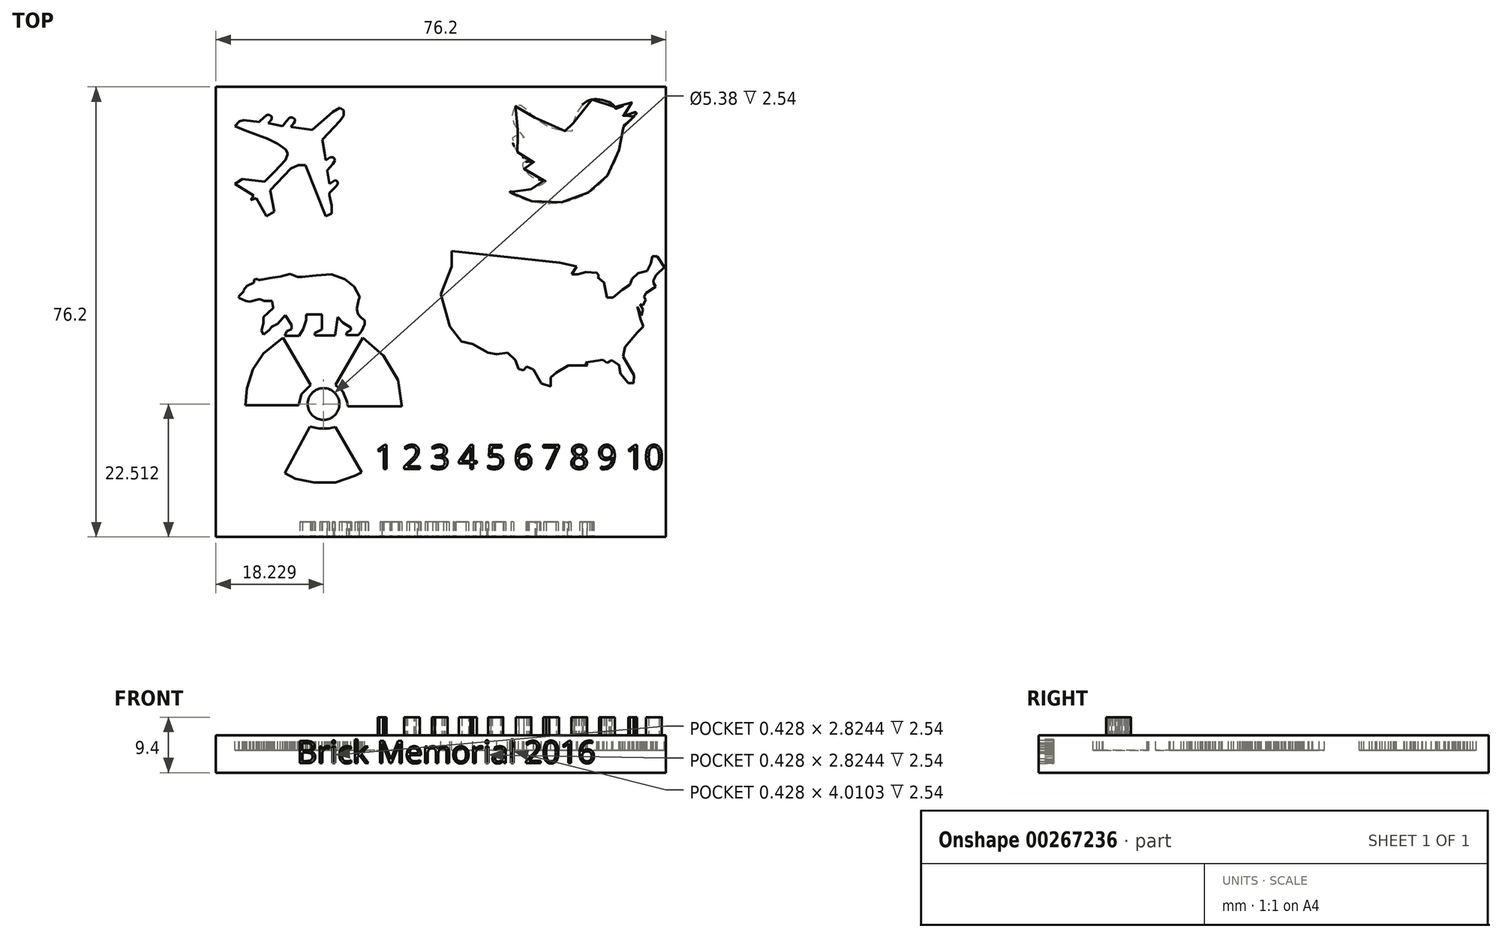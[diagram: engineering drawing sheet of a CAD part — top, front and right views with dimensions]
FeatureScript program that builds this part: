
annotation { "Feature Type Name" : "Feature", "Feature Type Description" : "" }
export const myFeature = defineFeature(function(context is Context, id is Id, definition is map)
    precondition{}
    {
        {
            var Q0;
            Q0=qCreatedBy(makeId("Top.planeOp"),FACE);
            var sketch = newSketch(context, id + "F0", { "sketchPlane" : qUnion([Q0])});
            skLineSegment(sketch, "E0.bottom", {"start": v(-38.1, 38.1) * mm, "end": v(38.1, 38.1) * mm});
            skLineSegment(sketch, "E0.top", {"start": v(-38.1, -38.1) * mm, "end": v(38.1, -38.1) * mm});
            skLineSegment(sketch, "E0.left", {"start": v(-38.1, 38.1) * mm, "end": v(-38.1, -38.1) * mm});
            skLineSegment(sketch, "E0.right", {"start": v(38.1, 38.1) * mm, "end": v(38.1, -38.1) * mm});
            skPoint(sketch, "E0.middle", {"position": v(0, 0) * mm});
            skSolve(sketch);
        }
        {
            var Q0;
            Q0 = qSketchRegion(id + "F0", true);
            extrude(context, id + "F1", {"entities" : qUnion([Q0]), "depth" : 6.35 * mm});
        }
        {
            var Q0;
            Q0=makeQuery(id+"F1.opExtrude","CAP_FACE",FACE,{"disambiguationData":[OSD([sQuery(id+"F0.wireOp",EDGE,"E0.bottom"),sQuery(id+"F0.wireOp",EDGE,"E0.top"),sQuery(id+"F0.wireOp",EDGE,"E0.left"),sQuery(id+"F0.wireOp",EDGE,"E0.right")])],"isStart":false});
            var sketch = newSketch(context, id + "F2", { "sketchPlane" : qUnion([Q0])});
            skLineSegment(sketch, "E1", {"start": v(-21.8, 30.81) * mm, "end": v(-25.4, 31.3) * mm});
            skLineSegment(sketch, "E2", {"start": v(-25.4, 31.3) * mm, "end": v(-24.89, 31.96) * mm});
            skLineSegment(sketch, "E3", {"start": v(-24.89, 31.96) * mm, "end": v(-24.72, 32.27) * mm});
            skLineSegment(sketch, "E4", {"start": v(-24.72, 32.27) * mm, "end": v(-24.72, 32.6) * mm});
            skLineSegment(sketch, "E5", {"start": v(-24.72, 32.6) * mm, "end": v(-25.07, 32.9) * mm});
            skLineSegment(sketch, "E6", {"start": v(-25.07, 32.9) * mm, "end": v(-25.61, 32.9) * mm});
            skLineSegment(sketch, "E7", {"start": v(-25.61, 32.9) * mm, "end": v(-26.16, 32.27) * mm});
            skLineSegment(sketch, "E8", {"start": v(-26.16, 32.27) * mm, "end": v(-26.78, 31.48) * mm});
            skLineSegment(sketch, "E9", {"start": v(-26.78, 31.48) * mm, "end": v(-29.25, 31.94) * mm});
            skLineSegment(sketch, "E10", {"start": v(-29.25, 31.94) * mm, "end": v(-28.62, 32.6) * mm});
            skLineSegment(sketch, "E11", {"start": v(-28.62, 32.6) * mm, "end": v(-28.62, 33.11) * mm});
            skLineSegment(sketch, "E12", {"start": v(-28.62, 33.11) * mm, "end": v(-29, 33.38) * mm});
            skLineSegment(sketch, "E13", {"start": v(-29, 33.38) * mm, "end": v(-29.47, 33.38) * mm});
            skLineSegment(sketch, "E14", {"start": v(-29.47, 33.38) * mm, "end": v(-30.68, 32.27) * mm});
            skLineSegment(sketch, "E15", {"start": v(-30.68, 32.27) * mm, "end": v(-30.68, 32.14) * mm});
            skLineSegment(sketch, "E16", {"start": v(-30.68, 32.14) * mm, "end": v(-33.35, 32.44) * mm});
            skLineSegment(sketch, "E17", {"start": v(-33.35, 32.44) * mm, "end": v(-34.1, 32.27) * mm});
            skLineSegment(sketch, "E18", {"start": v(-34.1, 32.27) * mm, "end": v(-34.87, 31.48) * mm});
            skLineSegment(sketch, "E19", {"start": v(-34.87, 31.48) * mm, "end": v(-33.2, 30.75) * mm});
            skLineSegment(sketch, "E20", {"start": v(-33.2, 30.75) * mm, "end": v(-29.3, 29.32) * mm});
            skLineSegment(sketch, "E21", {"start": v(-29.3, 29.32) * mm, "end": v(-27.64, 28.44) * mm});
            skLineSegment(sketch, "E22", {"start": v(-27.64, 28.44) * mm, "end": v(-26.3, 27.52) * mm});
            skLineSegment(sketch, "E23", {"start": v(-26.3, 27.52) * mm, "end": v(-25.89, 26.83) * mm});
            skLineSegment(sketch, "E24", {"start": v(-25.89, 26.83) * mm, "end": v(-26.3, 25.77) * mm});
            skLineSegment(sketch, "E25", {"start": v(-26.3, 25.77) * mm, "end": v(-28.15, 23.76) * mm});
            skLineSegment(sketch, "E26", {"start": v(-28.15, 23.76) * mm, "end": v(-29.87, 22.03) * mm});
            skLineSegment(sketch, "E27", {"start": v(-29.87, 22.03) * mm, "end": v(-33.63, 22.5) * mm});
            skLineSegment(sketch, "E28", {"start": v(-33.63, 22.5) * mm, "end": v(-34.87, 21.64) * mm});
            skLineSegment(sketch, "E29", {"start": v(-34.87, 21.64) * mm, "end": v(-31.71, 19.72) * mm});
            skLineSegment(sketch, "E30", {"start": v(-31.71, 19.72) * mm, "end": v(-32.19, 18.95) * mm});
            skLineSegment(sketch, "E31", {"start": v(-32.19, 18.95) * mm, "end": v(-31.27, 19.23) * mm});
            skLineSegment(sketch, "E32", {"start": v(-31.27, 19.23) * mm, "end": v(-29.55, 16.21) * mm});
            skLineSegment(sketch, "E33", {"start": v(-29.55, 16.21) * mm, "end": v(-28.2, 16.99) * mm});
            skLineSegment(sketch, "E34", {"start": v(-28.2, 16.99) * mm, "end": v(-28.9, 20.62) * mm});
            skLineSegment(sketch, "E35", {"start": v(-28.9, 20.62) * mm, "end": v(-25.44, 24.26) * mm});
            skLineSegment(sketch, "E36", {"start": v(-25.44, 24.26) * mm, "end": v(-24.16, 24.86) * mm});
            skLineSegment(sketch, "E37", {"start": v(-24.16, 24.86) * mm, "end": v(-22.96, 24.86) * mm});
            skLineSegment(sketch, "E38", {"start": v(-22.96, 24.86) * mm, "end": v(-19.5, 16.21) * mm});
            skLineSegment(sketch, "E39", {"start": v(-19.5, 16.21) * mm, "end": v(-18.47, 16.62) * mm});
            skLineSegment(sketch, "E40", {"start": v(-18.47, 16.62) * mm, "end": v(-18.47, 17.97) * mm});
            skLineSegment(sketch, "E41", {"start": v(-18.47, 17.97) * mm, "end": v(-18.9, 19.72) * mm});
            skLineSegment(sketch, "E42", {"start": v(-18.9, 19.72) * mm, "end": v(-18.9, 20.12) * mm});
            skLineSegment(sketch, "E43", {"start": v(-18.9, 20.12) * mm, "end": v(-17.83, 21.17) * mm});
            skLineSegment(sketch, "E44", {"start": v(-17.83, 21.17) * mm, "end": v(-17.48, 21.58) * mm});
            skLineSegment(sketch, "E45", {"start": v(-17.48, 21.58) * mm, "end": v(-17.48, 22.03) * mm});
            skLineSegment(sketch, "E46", {"start": v(-17.48, 22.03) * mm, "end": v(-17.93, 22.3) * mm});
            skLineSegment(sketch, "E47", {"start": v(-17.93, 22.3) * mm, "end": v(-18.9, 21.64) * mm});
            skLineSegment(sketch, "E48", {"start": v(-18.9, 21.64) * mm, "end": v(-19.26, 23.93) * mm});
            skLineSegment(sketch, "E49", {"start": v(-19.26, 23.93) * mm, "end": v(-18.3, 25.05) * mm});
            skLineSegment(sketch, "E50", {"start": v(-18.3, 25.05) * mm, "end": v(-17.93, 25.67) * mm});
            skLineSegment(sketch, "E51", {"start": v(-17.93, 25.67) * mm, "end": v(-18.15, 26.2) * mm});
            skLineSegment(sketch, "E52", {"start": v(-18.15, 26.2) * mm, "end": v(-18.74, 26.2) * mm});
            skLineSegment(sketch, "E53", {"start": v(-18.74, 26.2) * mm, "end": v(-19.5, 25.67) * mm});
            skLineSegment(sketch, "E54", {"start": v(-19.5, 25.67) * mm, "end": v(-19.7, 26.96) * mm});
            skLineSegment(sketch, "E55", {"start": v(-19.7, 26.96) * mm, "end": v(-20.1, 29.15) * mm});
            skLineSegment(sketch, "E56", {"start": v(-20.1, 29.15) * mm, "end": v(-17.12, 32.33) * mm});
            skLineSegment(sketch, "E57", {"start": v(-17.12, 32.33) * mm, "end": v(-16.47, 33.21) * mm});
            skLineSegment(sketch, "E58", {"start": v(-16.47, 33.21) * mm, "end": v(-16.47, 34.1) * mm});
            skLineSegment(sketch, "E59", {"start": v(-16.47, 34.1) * mm, "end": v(-17.12, 34.58) * mm});
            skLineSegment(sketch, "E60", {"start": v(-17.12, 34.58) * mm, "end": v(-18.3, 33.83) * mm});
            skLineSegment(sketch, "E61", {"start": v(-18.3, 33.83) * mm, "end": v(-21.8, 30.81) * mm});
            skPoint(sketch, "E62.14.internal.snap0", {"position": v(22.23, 18.37) * mm});
            skPoint(sketch, "E62.15.internal.snap0", {"position": v(22.23, 18.37) * mm});
            skFitSpline(sketch, "E62", {"points": [v(11.66, 20.28) * mm, v(15.22, 18.75) * mm, v(21.58, 18.78) * mm, v(26.37, 21.18) * mm, v(29.2, 24.8) * mm, v(30.81, 30.2) * mm, v(31.01, 31.68) * mm, v(31.25, 31.8) * mm, v(33.08, 33.8) * mm, v(30.85, 33.24) * mm, v(32.41, 35.44) * mm, v(29.66, 34.44) * mm, v(29.34, 34.88) * mm, v(24.58, 35.6) * mm, v(22.23, 30.76) * mm, v(22.23, 30.6) * mm, v(17.5, 31.68) * mm, v(13.07, 35.04) * mm, v(12.23, 32.2) * mm, v(14.07, 29.48) * mm, v(12.35, 29.76) * mm, v(13.63, 26.36) * mm, v(15.75, 25.36) * mm, v(13.95, 25.24) * mm, v(15.66, 22.76) * mm, v(17.74, 22.1) * mm, v(14.42, 20.6) * mm, v(11.66, 20.28) * mm]});
            skLineSegment(sketch, "E63", {"start": v(-19.66, -20.7) * mm, "end": v(-27.1, -20.7) * mm});
            skLineSegment(sketch, "E64", {"start": v(-27.1, -20.7) * mm, "end": v(-27.47, -20.99) * mm});
            skLineSegment(sketch, "E65", {"start": v(-27.47, -20.99) * mm, "end": v(-27.47, -21.5) * mm});
            skLineSegment(sketch, "E66", {"start": v(-27.47, -21.5) * mm, "end": v(-27.33, -21.8) * mm});
            skLineSegment(sketch, "E67", {"start": v(-27.33, -21.8) * mm, "end": v(-26.74, -21.95) * mm});
            skLineSegment(sketch, "E68", {"start": v(-26.74, -21.95) * mm, "end": v(-26.97, -25.9) * mm});
            skLineSegment(sketch, "E69", {"start": v(-26.97, -25.9) * mm, "end": v(-27.9, -26.04) * mm});
            skLineSegment(sketch, "E70", {"start": v(-27.9, -26.04) * mm, "end": v(-28.25, -26.27) * mm});
            skLineSegment(sketch, "E71", {"start": v(-28.25, -26.27) * mm, "end": v(-28.41, -26.6) * mm});
            skLineSegment(sketch, "E72", {"start": v(-28.41, -26.6) * mm, "end": v(-28.41, -27.5) * mm});
            skLineSegment(sketch, "E73", {"start": v(-28.39, -27.5) * mm, "end": v(-29.75, -33.23) * mm});
            skLineSegment(sketch, "E74", {"start": v(-29.75, -33.23) * mm, "end": v(-30.9, -33.23) * mm});
            skLineSegment(sketch, "E75", {"start": v(-30.9, -33.23) * mm, "end": v(-30.9, -34.32) * mm});
            skLineSegment(sketch, "E76", {"start": v(-30.9, -34.32) * mm, "end": v(-9.68, -34.32) * mm});
            skLineSegment(sketch, "E77", {"start": v(-9.68, -34.32) * mm, "end": v(-11.16, -14.82) * mm});
            skLineSegment(sketch, "E78", {"start": v(-11.16, -14.82) * mm, "end": v(-10.96, -14.71) * mm});
            skLineSegment(sketch, "E79", {"start": v(-10.96, -14.71) * mm, "end": v(-10.87, -14.56) * mm});
            skLineSegment(sketch, "E80", {"start": v(-10.87, -14.56) * mm, "end": v(-10.87, -14.08) * mm});
            skLineSegment(sketch, "E81", {"start": v(-10.87, -14.08) * mm, "end": v(-10.96, -13.84) * mm});
            skLineSegment(sketch, "E82", {"start": v(-10.96, -13.84) * mm, "end": v(-12.62, -13.84) * mm});
            skLineSegment(sketch, "E83", {"start": v(-12.62, -13.84) * mm, "end": v(-12.62, -13.57) * mm});
            skLineSegment(sketch, "E84", {"start": v(-12.62, -13.57) * mm, "end": v(-11.74, -13.26) * mm});
            skLineSegment(sketch, "E85", {"start": v(-11.74, -13.26) * mm, "end": v(-11.47, -13) * mm});
            skLineSegment(sketch, "E86", {"start": v(-11.47, -13) * mm, "end": v(-10.96, -12.68) * mm});
            skLineSegment(sketch, "E87", {"start": v(-10.96, -12.68) * mm, "end": v(-10.44, -12.68) * mm});
            skLineSegment(sketch, "E88", {"start": v(-10.44, -12.68) * mm, "end": v(-9.68, -12.35) * mm});
            skLineSegment(sketch, "E89", {"start": v(-9.68, -12.35) * mm, "end": v(-9.68, -11.67) * mm});
            skLineSegment(sketch, "E90", {"start": v(-9.68, -11.67) * mm, "end": v(-9.97, -11.32) * mm});
            skLineSegment(sketch, "E91", {"start": v(-9.97, -11.32) * mm, "end": v(-9.68, -11.08) * mm});
            skLineSegment(sketch, "E92", {"start": v(-9.68, -11.08) * mm, "end": v(-9.12, -11.47) * mm});
            skLineSegment(sketch, "E93", {"start": v(-9.12, -11.47) * mm, "end": v(-8.46, -11.26) * mm});
            skLineSegment(sketch, "E94", {"start": v(-8.46, -11.26) * mm, "end": v(-8.46, -10.83) * mm});
            skLineSegment(sketch, "E95", {"start": v(-8.46, -10.83) * mm, "end": v(-7.97, -10.83) * mm});
            skLineSegment(sketch, "E96", {"start": v(-7.97, -10.83) * mm, "end": v(-7.66, -10.56) * mm});
            skLineSegment(sketch, "E97", {"start": v(-7.66, -10.56) * mm, "end": v(-7.66, -10.27) * mm});
            skLineSegment(sketch, "E98", {"start": v(-7.66, -10.27) * mm, "end": v(-7.41, -9.84) * mm});
            skLineSegment(sketch, "E99", {"start": v(-7.41, -9.84) * mm, "end": v(-6.88, -9.84) * mm});
            skLineSegment(sketch, "E100", {"start": v(-6.88, -9.84) * mm, "end": v(-6.67, -9.22) * mm});
            skLineSegment(sketch, "E101", {"start": v(-6.67, -9.22) * mm, "end": v(-6.67, -8.77) * mm});
            skLineSegment(sketch, "E102", {"start": v(-6.67, -8.77) * mm, "end": v(-6.26, -8.4) * mm});
            skLineSegment(sketch, "E103", {"start": v(-6.26, -8.4) * mm, "end": v(-6.26, -7.7) * mm});
            skLineSegment(sketch, "E104", {"start": v(-6.26, -7.7) * mm, "end": v(-6.94, -7.1) * mm});
            skLineSegment(sketch, "E105", {"start": v(-6.94, -7.1) * mm, "end": v(-7.25, -7.1) * mm});
            skLineSegment(sketch, "E106", {"start": v(-7.25, -7.1) * mm, "end": v(-7.25, -6.54) * mm});
            skLineSegment(sketch, "E107", {"start": v(-7.25, -6.54) * mm, "end": v(-7.66, -6.1) * mm});
            skLineSegment(sketch, "E108", {"start": v(-7.66, -6.1) * mm, "end": v(-8.26, -6.1) * mm});
            skLineSegment(sketch, "E109", {"start": v(-8.26, -6.1) * mm, "end": v(-8.96, -5.68) * mm});
            skLineSegment(sketch, "E110", {"start": v(-8.96, -5.68) * mm, "end": v(-10.15, -5.5) * mm});
            skLineSegment(sketch, "E111", {"start": v(-10.15, -5.5) * mm, "end": v(-11.16, -5.93) * mm});
            skLineSegment(sketch, "E112", {"start": v(-11.16, -5.93) * mm, "end": v(-11.82, -6.24) * mm});
            skLineSegment(sketch, "E113", {"start": v(-11.82, -6.24) * mm, "end": v(-11.82, -6.77) * mm});
            skLineSegment(sketch, "E114", {"start": v(-11.82, -6.77) * mm, "end": v(-11.68, -7.1) * mm});
            skLineSegment(sketch, "E115", {"start": v(-11.68, -7.1) * mm, "end": v(-12.19, -7.32) * mm});
            skLineSegment(sketch, "E116", {"start": v(-12.19, -7.32) * mm, "end": v(-12.21, -7.43) * mm});
            skLineSegment(sketch, "E117", {"start": v(-12.21, -7.43) * mm, "end": v(-11.99, -7.97) * mm});
            skLineSegment(sketch, "E118", {"start": v(-11.99, -7.97) * mm, "end": v(-12.91, -7.68) * mm});
            skLineSegment(sketch, "E119", {"start": v(-12.91, -7.68) * mm, "end": v(-13.74, -8.13) * mm});
            skLineSegment(sketch, "E120", {"start": v(-13.74, -8.13) * mm, "end": v(-13.74, -9.06) * mm});
            skLineSegment(sketch, "E121", {"start": v(-13.74, -9.06) * mm, "end": v(-14.27, -9.32) * mm});
            skLineSegment(sketch, "E122", {"start": v(-14.27, -9.32) * mm, "end": v(-14.27, -9.65) * mm});
            skLineSegment(sketch, "E123", {"start": v(-14.27, -9.65) * mm, "end": v(-14.83, -10.33) * mm});
            skLineSegment(sketch, "E124", {"start": v(-14.83, -10.33) * mm, "end": v(-14.64, -11.08) * mm});
            skLineSegment(sketch, "E125", {"start": v(-14.64, -11.08) * mm, "end": v(-13.96, -11.59) * mm});
            skLineSegment(sketch, "E126", {"start": v(-13.96, -11.59) * mm, "end": v(-14.36, -12.12) * mm});
            skLineSegment(sketch, "E127", {"start": v(-14.36, -12.12) * mm, "end": v(-13.74, -13) * mm});
            skLineSegment(sketch, "E128", {"start": v(-13.74, -13) * mm, "end": v(-13.08, -13.57) * mm});
            skLineSegment(sketch, "E129", {"start": v(-13.08, -13.57) * mm, "end": v(-13.08, -13.84) * mm});
            skLineSegment(sketch, "E130", {"start": v(-13.08, -13.84) * mm, "end": v(-14.85, -13.84) * mm});
            skLineSegment(sketch, "E131", {"start": v(-14.85, -13.84) * mm, "end": v(-14.94, -14.08) * mm});
            skLineSegment(sketch, "E132", {"start": v(-14.94, -14.08) * mm, "end": v(-14.94, -14.52) * mm});
            skLineSegment(sketch, "E133", {"start": v(-14.94, -14.52) * mm, "end": v(-14.85, -14.82) * mm});
            skLineSegment(sketch, "E134", {"start": v(-14.85, -14.82) * mm, "end": v(-14.48, -14.71) * mm});
            skLineSegment(sketch, "E135", {"start": v(-14.48, -14.71) * mm, "end": v(-15.3, -24.74) * mm});
            skLineSegment(sketch, "E136", {"start": v(-15.3, -24.74) * mm, "end": v(-19.66, -24.74) * mm});
            skLineSegment(sketch, "E137", {"start": v(-19.66, -24.74) * mm, "end": v(-20.21, -22.11) * mm});
            skLineSegment(sketch, "E138", {"start": v(-20.21, -22.11) * mm, "end": v(-19.66, -22) * mm});
            skLineSegment(sketch, "E139", {"start": v(-19.66, -22) * mm, "end": v(-19.34, -21.46) * mm});
            skLineSegment(sketch, "E140", {"start": v(-19.34, -21.46) * mm, "end": v(-19.66, -20.7) * mm});
            skLineSegment(sketch, "E141", {"start": v(28.14, 2.4) * mm, "end": v(29.15, 2.4) * mm});
            skLineSegment(sketch, "E142", {"start": v(29.15, 2.4) * mm, "end": v(30.7, 3.79) * mm});
            skLineSegment(sketch, "E143", {"start": v(30.7, 3.79) * mm, "end": v(31.98, 4.61) * mm});
            skLineSegment(sketch, "E144", {"start": v(31.98, 4.61) * mm, "end": v(32.4, 5.57) * mm});
            skLineSegment(sketch, "E145", {"start": v(32.4, 5.57) * mm, "end": v(33.4, 6.59) * mm});
            skLineSegment(sketch, "E146", {"start": v(33.4, 6.59) * mm, "end": v(34.91, 6.9) * mm});
            skLineSegment(sketch, "E147", {"start": v(34.91, 6.9) * mm, "end": v(35.52, 8.24) * mm});
            skLineSegment(sketch, "E148", {"start": v(35.52, 8.24) * mm, "end": v(35.82, 9.44) * mm});
            skLineSegment(sketch, "E149", {"start": v(35.82, 9.44) * mm, "end": v(36.62, 9.44) * mm});
            skLineSegment(sketch, "E150", {"start": v(36.62, 9.44) * mm, "end": v(37.82, 7.6) * mm});
            skLineSegment(sketch, "E151", {"start": v(37.82, 7.6) * mm, "end": v(36.43, 6.21) * mm});
            skLineSegment(sketch, "E152", {"start": v(36.43, 6.21) * mm, "end": v(36, 5.36) * mm});
            skLineSegment(sketch, "E153", {"start": v(36, 5.36) * mm, "end": v(36, 4.9) * mm});
            skLineSegment(sketch, "E154", {"start": v(36, 4.9) * mm, "end": v(36.4, 4.3) * mm});
            skLineSegment(sketch, "E155", {"start": v(36.4, 4.3) * mm, "end": v(34.7, 3.18) * mm});
            skLineSegment(sketch, "E156", {"start": v(34.7, 3.18) * mm, "end": v(34.4, 2.59) * mm});
            skLineSegment(sketch, "E157", {"start": v(34.4, 2.59) * mm, "end": v(34.64, 2.03) * mm});
            skLineSegment(sketch, "E158", {"start": v(34.64, 2.03) * mm, "end": v(34.24, 1.07) * mm});
            skLineSegment(sketch, "E159", {"start": v(34.24, 1.07) * mm, "end": v(33.72, 1.29) * mm});
            skLineSegment(sketch, "E160", {"start": v(33.72, 1.29) * mm, "end": v(34.24, 0.4) * mm});
            skLineSegment(sketch, "E161", {"start": v(34.24, 0.4) * mm, "end": v(33.95, -0.6) * mm});
            skLineSegment(sketch, "E162", {"start": v(33.95, -0.6) * mm, "end": v(33.28, 0.94) * mm});
            skLineSegment(sketch, "E163", {"start": v(33.28, 0.94) * mm, "end": v(33.84, -1.3) * mm});
            skLineSegment(sketch, "E164", {"start": v(33.84, -1.3) * mm, "end": v(34.3, -2.45) * mm});
            skLineSegment(sketch, "E165", {"start": v(34.3, -2.45) * mm, "end": v(33.28, -3.49) * mm});
            skLineSegment(sketch, "E166", {"start": v(33.28, -3.49) * mm, "end": v(31.18, -5.93) * mm});
            skLineSegment(sketch, "E167", {"start": v(31.18, -5.93) * mm, "end": v(30.82, -7.54) * mm});
            skLineSegment(sketch, "E168", {"start": v(30.82, -7.54) * mm, "end": v(32.7, -10.73) * mm});
            skLineSegment(sketch, "E169", {"start": v(32.7, -10.73) * mm, "end": v(32.63, -12.07) * mm});
            skLineSegment(sketch, "E170", {"start": v(32.63, -12.07) * mm, "end": v(31.77, -12.07) * mm});
            skLineSegment(sketch, "E171", {"start": v(31.77, -12.07) * mm, "end": v(30.4, -10.5) * mm});
            skLineSegment(sketch, "E172", {"start": v(30.4, -10.5) * mm, "end": v(30.13, -8.98) * mm});
            skLineSegment(sketch, "E173", {"start": v(30.13, -8.98) * mm, "end": v(28.92, -8.17) * mm});
            skLineSegment(sketch, "E174", {"start": v(28.92, -8.17) * mm, "end": v(28.14, -8.63) * mm});
            skLineSegment(sketch, "E175", {"start": v(28.14, -8.63) * mm, "end": v(27.4, -8.1) * mm});
            skLineSegment(sketch, "E176", {"start": v(27.4, -8.1) * mm, "end": v(24.5, -8.54) * mm});
            skLineSegment(sketch, "E177", {"start": v(24.5, -8.54) * mm, "end": v(24.8, -9.06) * mm});
            skLineSegment(sketch, "E178", {"start": v(24.8, -9.06) * mm, "end": v(21.55, -9.06) * mm});
            skLineSegment(sketch, "E179", {"start": v(21.55, -9.06) * mm, "end": v(19.55, -10.24) * mm});
            skLineSegment(sketch, "E180", {"start": v(19.55, -10.24) * mm, "end": v(18.58, -11.11) * mm});
            skLineSegment(sketch, "E181", {"start": v(18.58, -11.11) * mm, "end": v(18.58, -12.6) * mm});
            skLineSegment(sketch, "E182", {"start": v(18.58, -12.6) * mm, "end": v(17.04, -12.1) * mm});
            skLineSegment(sketch, "E183", {"start": v(17.04, -12.1) * mm, "end": v(15.65, -9.76) * mm});
            skLineSegment(sketch, "E184", {"start": v(15.65, -9.76) * mm, "end": v(14.53, -9.28) * mm});
            skLineSegment(sketch, "E185", {"start": v(14.53, -9.28) * mm, "end": v(13.97, -9.87) * mm});
            skLineSegment(sketch, "E186", {"start": v(13.97, -9.87) * mm, "end": v(13.17, -9.63) * mm});
            skLineSegment(sketch, "E187", {"start": v(13.17, -9.63) * mm, "end": v(12.64, -8.2) * mm});
            skLineSegment(sketch, "E188", {"start": v(12.64, -8.2) * mm, "end": v(11.31, -6.93) * mm});
            skLineSegment(sketch, "E189", {"start": v(11.31, -6.93) * mm, "end": v(9.45, -7.16) * mm});
            skLineSegment(sketch, "E190", {"start": v(9.45, -7.16) * mm, "end": v(7.99, -6.93) * mm});
            skLineSegment(sketch, "E191", {"start": v(7.99, -6.93) * mm, "end": v(5.39, -5.45) * mm});
            skLineSegment(sketch, "E192", {"start": v(5.39, -5.45) * mm, "end": v(3.49, -5.02) * mm});
            skLineSegment(sketch, "E193", {"start": v(3.49, -5.02) * mm, "end": v(1.54, -2.47) * mm});
            skLineSegment(sketch, "E194", {"start": v(1.54, -2.47) * mm, "end": v(0, 3.02) * mm});
            skLineSegment(sketch, "E195", {"start": v(0, 3.02) * mm, "end": v(1.8, 7.7) * mm});
            skLineSegment(sketch, "E196", {"start": v(1.8, 7.7) * mm, "end": v(1.8, 10.3) * mm});
            skLineSegment(sketch, "E197", {"start": v(1.8, 10.3) * mm, "end": v(20.15, 8.32) * mm});
            skLineSegment(sketch, "E198", {"start": v(20.15, 8.32) * mm, "end": v(22.96, 7.7) * mm});
            skLineSegment(sketch, "E199", {"start": v(22.96, 7.7) * mm, "end": v(22.14, 6.34) * mm});
            skLineSegment(sketch, "E200", {"start": v(22.14, 6.34) * mm, "end": v(23.19, 6.34) * mm});
            skLineSegment(sketch, "E201", {"start": v(23.19, 6.34) * mm, "end": v(24.56, 6.72) * mm});
            skLineSegment(sketch, "E202", {"start": v(24.56, 6.72) * mm, "end": v(26.38, 6.61) * mm});
            skLineSegment(sketch, "E203", {"start": v(26.38, 6.61) * mm, "end": v(26.77, 6.06) * mm});
            skLineSegment(sketch, "E204", {"start": v(26.77, 6.06) * mm, "end": v(25.27, 5.01) * mm});
            skLineSegment(sketch, "E205", {"start": v(25.27, 5.01) * mm, "end": v(25.27, 2.1) * mm});
            skLineSegment(sketch, "E206", {"start": v(25.27, 2.1) * mm, "end": v(25.94, 4.08) * mm});
            skLineSegment(sketch, "E207", {"start": v(25.94, 4.08) * mm, "end": v(26.52, 5.89) * mm});
            skLineSegment(sketch, "E208", {"start": v(26.52, 5.89) * mm, "end": v(27.6, 4.96) * mm});
            skLineSegment(sketch, "E209", {"start": v(27.6, 4.96) * mm, "end": v(28.14, 2.4) * mm});
            skSolve(sketch);
        }
        {
            var Q0;
            Q0 = qSketchRegion(id + "F2", true);
            extrude(context, id + "F3", {"entities" : qUnion([Q0]), "operationType" : NewBodyOperationType.REMOVE, "oppositeDirection" : true, "depth" : 2.54 * mm});
        }
        {
            var Q0;
            Q0=makeQuery(id+"F1.opExtrude","CAP_FACE",FACE,{"disambiguationData":[OSD([sQuery(id+"F0.wireOp",EDGE,"E0.bottom"),sQuery(id+"F0.wireOp",EDGE,"E0.top"),sQuery(id+"F0.wireOp",EDGE,"E0.left"),sQuery(id+"F0.wireOp",EDGE,"E0.right")])],"isStart":false});
            var sketch = newSketch(context, id + "F4", { "sketchPlane" : qUnion([Q0])});
            skLineSegment(sketch, "E210", {"start": v(-22.04, -12.38) * mm, "end": v(-26.72, -4.34) * mm});
            skLineSegment(sketch, "E211", {"start": v(-33.12, -15.8) * mm, "end": v(-24.06, -15.8) * mm});
            skLineSegment(sketch, "E212", {"start": v(-26.72, -4.34) * mm, "end": v(-30.01, -7.06) * mm});
            skLineSegment(sketch, "E213", {"start": v(-30.01, -7.06) * mm, "end": v(-31.85, -9.72) * mm});
            skLineSegment(sketch, "E214", {"start": v(-31.85, -9.72) * mm, "end": v(-32.86, -12.95) * mm});
            skLineSegment(sketch, "E215", {"start": v(-32.86, -12.95) * mm, "end": v(-33.12, -15.8) * mm});
            skLineSegment(sketch, "E216", {"start": v(-24.06, -15.8) * mm, "end": v(-23.62, -13.96) * mm});
            skLineSegment(sketch, "E217", {"start": v(-23.62, -13.96) * mm, "end": v(-22.04, -12.38) * mm});
            skLineSegment(sketch, "E218", {"start": v(-17.86, -12.38) * mm, "end": v(-13.24, -4.34) * mm});
            skLineSegment(sketch, "E219", {"start": v(-13.24, -4.34) * mm, "end": v(-9.7, -7.44) * mm});
            skLineSegment(sketch, "E220", {"start": v(-9.7, -7.44) * mm, "end": v(-7.23, -11.55) * mm});
            skLineSegment(sketch, "E221", {"start": v(-7.23, -11.55) * mm, "end": v(-6.6, -15.98) * mm});
            skLineSegment(sketch, "E222", {"start": v(-6.6, -15.98) * mm, "end": v(-15.77, -15.98) * mm});
            skLineSegment(sketch, "E223", {"start": v(-17.86, -12.38) * mm, "end": v(-16.58, -13.5) * mm});
            skLineSegment(sketch, "E224", {"start": v(-16.58, -13.5) * mm, "end": v(-15.88, -15.21) * mm});
            skLineSegment(sketch, "E225", {"start": v(-15.88, -15.21) * mm, "end": v(-15.77, -15.98) * mm});
            skLineSegment(sketch, "E226", {"start": v(-17.86, -19.46) * mm, "end": v(-13.44, -27.14) * mm});
            skLineSegment(sketch, "E227", {"start": v(-13.44, -27.14) * mm, "end": v(-14.52, -27.76) * mm});
            skLineSegment(sketch, "E228", {"start": v(-14.52, -27.76) * mm, "end": v(-17.86, -28.87) * mm});
            skLineSegment(sketch, "E229", {"start": v(-17.86, -28.87) * mm, "end": v(-21.5, -28.87) * mm});
            skLineSegment(sketch, "E230", {"start": v(-21.5, -28.87) * mm, "end": v(-24.64, -28.25) * mm});
            skLineSegment(sketch, "E231", {"start": v(-24.64, -28.25) * mm, "end": v(-26.43, -27.28) * mm});
            skLineSegment(sketch, "E232", {"start": v(-26.43, -27.28) * mm, "end": v(-22.16, -19.38) * mm});
            skLineSegment(sketch, "E233", {"start": v(-17.86, -19.46) * mm, "end": v(-18.98, -19.7) * mm});
            skLineSegment(sketch, "E234", {"start": v(-18.98, -19.7) * mm, "end": v(-20.66, -19.7) * mm});
            skLineSegment(sketch, "E235", {"start": v(-20.66, -19.7) * mm, "end": v(-22.16, -19.38) * mm});
            skCircle(sketch, "E236", {"center": v(-19.87, -15.59) * mm, "radius": 2.69 * mm});
            skSolve(sketch);
        }
        {
            var Q0;
            Q0 = qSketchRegion(id + "F4", true);
            extrude(context, id + "F5", {"entities" : qUnion([Q0]), "operationType" : NewBodyOperationType.REMOVE, "oppositeDirection" : true, "depth" : 2.54 * mm});
        }
        {
            var Q0;
            Q0=makeQuery(id+"F1.opExtrude","SWEPT_FACE",FACE,{"disambiguationData":[OSD([sQuery(id+"F0.wireOp",EDGE,"E0.top")])]});
            var sketch = newSketch(context, id + "F6", { "sketchPlane" : qUnion([Q0])});
            skText(sketch, "E237", { "text": "Brick Memorial 2016", "fontName": "OpenSans-Regular.ttf"});
            const initialGuessF6  = {"E237": [-0.0244, 0.0016, 1, 0, 0.0038]};
            skSetInitialGuess(sketch, initialGuessF6);
            skSolve(sketch);
        }
        {
            var Q0;
            Q0 = qSketchRegion(id + "F6", true);
            extrude(context, id + "F7", {"entities" : qUnion([Q0]), "operationType" : NewBodyOperationType.REMOVE, "oppositeDirection" : true, "depth" : 2.54 * mm});
        }
        {
            var Q0;
            Q0=makeQuery(id+"F1.opExtrude","CAP_FACE",FACE,{"disambiguationData":[OSD([sQuery(id+"F0.wireOp",EDGE,"E0.bottom"),sQuery(id+"F0.wireOp",EDGE,"E0.top"),sQuery(id+"F0.wireOp",EDGE,"E0.left"),sQuery(id+"F0.wireOp",EDGE,"E0.right")])],"isStart":false});
            var sketch = newSketch(context, id + "F8", { "sketchPlane" : qUnion([Q0])});
            skText(sketch, "E238", { "text": "1 2 3 4 5 6 7 8 9 10", "fontName": "OpenSans-Regular.ttf"});
            const initialGuessF8  = {"E238": [-0.0112, -0.02658, 1, 0, 0.00408]};
            skSetInitialGuess(sketch, initialGuessF8);
            skSolve(sketch);
        }
        {
            var Q0;
            Q0 = qSketchRegion(id + "F8", true);
            extrude(context, id + "F9", {"entities" : qUnion([Q0]), "operationType" : NewBodyOperationType.ADD, "depth" : 3.05 * mm});
        }
        {
            var Q0;
            {var subQ0=sQuery(id+"F0.wireOp",EDGE,"E0.top");var subQ1=sQuery(id+"F0.wireOp",EDGE,"E0.left");var subQ2=sQuery(id+"F0.wireOp",EDGE,"E0.right");var subQ3=sQuery(id+"F0.wireOp",EDGE,"E0.bottom");Q0=makeQuery(id+"F9.boolean.opBoolean","SPLIT",FACE,{"disambiguationData":[TD([makeQuery(id+"F1.opExtrude","SWEPT_FACE",FACE,{"disambiguationData":[OSD([subQ3])]})])],"derivedFrom":makeQuery(id+"F1.opExtrude","CAP_FACE",FACE,{"disambiguationData":[OSD([subQ3,subQ0,subQ1,subQ2])],"isStart":false})});}
            var sketch = newSketch(context, id + "F10", { "sketchPlane" : qUnion([Q0])});
            skLineSegment(sketch, "E239", {"start": v(-31.63, 5) * mm, "end": v(-32.8, 4.42) * mm});
            skLineSegment(sketch, "E240", {"start": v(-32.8, 4.42) * mm, "end": v(-33.39, 3.7) * mm});
            skLineSegment(sketch, "E241", {"start": v(-33.39, 3.7) * mm, "end": v(-33.35, 3.5) * mm});
            skLineSegment(sketch, "E242", {"start": v(-33.35, 3.5) * mm, "end": v(-34.24, 2.62) * mm});
            skLineSegment(sketch, "E243", {"start": v(-34.24, 2.62) * mm, "end": v(-34.18, 2.34) * mm});
            skLineSegment(sketch, "E244", {"start": v(-34.18, 2.34) * mm, "end": v(-33.06, 1.85) * mm});
            skLineSegment(sketch, "E245", {"start": v(-33.06, 1.85) * mm, "end": v(-32.4, 1.74) * mm});
            skLineSegment(sketch, "E246", {"start": v(-32.4, 1.74) * mm, "end": v(-30.65, 2.14) * mm});
            skLineSegment(sketch, "E247", {"start": v(-30.65, 2.14) * mm, "end": v(-29.93, 1.85) * mm});
            skLineSegment(sketch, "E248", {"start": v(-29.93, 1.85) * mm, "end": v(-28.56, 1.85) * mm});
            skLineSegment(sketch, "E249", {"start": v(-28.56, 1.85) * mm, "end": v(-28.39, 0.65) * mm});
            skLineSegment(sketch, "E250", {"start": v(-28.39, 0.65) * mm, "end": v(-30.01, -0.88) * mm});
            skLineSegment(sketch, "E251", {"start": v(-30.01, -0.88) * mm, "end": v(-30.01, -1.88) * mm});
            skLineSegment(sketch, "E252", {"start": v(-30.01, -1.88) * mm, "end": v(-30.36, -3.16) * mm});
            skLineSegment(sketch, "E253", {"start": v(-30.36, -3.16) * mm, "end": v(-30.01, -3.88) * mm});
            skLineSegment(sketch, "E254", {"start": v(-30.01, -3.88) * mm, "end": v(-29.05, -3.05) * mm});
            skLineSegment(sketch, "E255", {"start": v(-29.05, -3.05) * mm, "end": v(-28.67, -2.5) * mm});
            skLineSegment(sketch, "E256", {"start": v(-28.67, -2.5) * mm, "end": v(-27.6, -1.99) * mm});
            skLineSegment(sketch, "E257", {"start": v(-27.6, -1.99) * mm, "end": v(-26.37, -0.57) * mm});
            skLineSegment(sketch, "E258", {"start": v(-26.37, -0.57) * mm, "end": v(-25.3, -2.2) * mm});
            skLineSegment(sketch, "E259", {"start": v(-25.3, -2.2) * mm, "end": v(-25.3, -2.92) * mm});
            skLineSegment(sketch, "E260", {"start": v(-25.3, -2.92) * mm, "end": v(-26.1, -3.26) * mm});
            skLineSegment(sketch, "E261", {"start": v(-26.1, -3.26) * mm, "end": v(-26.43, -4.02) * mm});
            skLineSegment(sketch, "E262", {"start": v(-26.43, -4.02) * mm, "end": v(-24.02, -4.02) * mm});
            skLineSegment(sketch, "E263", {"start": v(-24.02, -4.02) * mm, "end": v(-23.33, -2.88) * mm});
            skLineSegment(sketch, "E264", {"start": v(-23.33, -2.88) * mm, "end": v(-22.78, -1.37) * mm});
            skLineSegment(sketch, "E265", {"start": v(-22.78, -1.37) * mm, "end": v(-22.78, -0.4) * mm});
            skLineSegment(sketch, "E266", {"start": v(-22.78, -0.4) * mm, "end": v(-20.13, -0.4) * mm});
            skLineSegment(sketch, "E267", {"start": v(-20.13, -0.4) * mm, "end": v(-20.13, -2.99) * mm});
            skLineSegment(sketch, "E268", {"start": v(-20.13, -2.99) * mm, "end": v(-21.44, -3.57) * mm});
            skLineSegment(sketch, "E269", {"start": v(-21.44, -3.57) * mm, "end": v(-21.26, -3.97) * mm});
            skLineSegment(sketch, "E270", {"start": v(-21.26, -3.97) * mm, "end": v(-17.93, -3.97) * mm});
            skLineSegment(sketch, "E271", {"start": v(-17.93, -3.97) * mm, "end": v(-17.48, -0.88) * mm});
            skLineSegment(sketch, "E272", {"start": v(-17.48, -0.88) * mm, "end": v(-16.58, -1.85) * mm});
            skLineSegment(sketch, "E273", {"start": v(-16.58, -1.85) * mm, "end": v(-15.24, -2.64) * mm});
            skLineSegment(sketch, "E274", {"start": v(-15.24, -2.64) * mm, "end": v(-15.24, -3.09) * mm});
            skLineSegment(sketch, "E275", {"start": v(-15.24, -3.09) * mm, "end": v(-15.93, -3.47) * mm});
            skLineSegment(sketch, "E276", {"start": v(-15.93, -3.47) * mm, "end": v(-16, -3.95) * mm});
            skLineSegment(sketch, "E277", {"start": v(-16, -3.95) * mm, "end": v(-14, -3.95) * mm});
            skLineSegment(sketch, "E278", {"start": v(-14, -3.95) * mm, "end": v(-13.39, -3.25) * mm});
            skLineSegment(sketch, "E279", {"start": v(-13.39, -3.25) * mm, "end": v(-12.9, -2.1) * mm});
            skLineSegment(sketch, "E280", {"start": v(-12.9, -2.1) * mm, "end": v(-12.9, -1.45) * mm});
            skLineSegment(sketch, "E281", {"start": v(-12.9, -1.45) * mm, "end": v(-13.56, -0.96) * mm});
            skLineSegment(sketch, "E282", {"start": v(-13.56, -0.96) * mm, "end": v(-14.04, -0.34) * mm});
            skLineSegment(sketch, "E283", {"start": v(-14.04, -0.34) * mm, "end": v(-14.26, 0.53) * mm});
            skLineSegment(sketch, "E284", {"start": v(-14.26, 0.53) * mm, "end": v(-13.91, 2.11) * mm});
            skLineSegment(sketch, "E285", {"start": v(-13.91, 2.11) * mm, "end": v(-13.75, 2.5) * mm});
            skLineSegment(sketch, "E286", {"start": v(-13.75, 2.5) * mm, "end": v(-14.67, 4.3) * mm});
            skLineSegment(sketch, "E287", {"start": v(-14.67, 4.3) * mm, "end": v(-16.24, 5.56) * mm});
            skLineSegment(sketch, "E288", {"start": v(-16.24, 5.56) * mm, "end": v(-18.57, 6.4) * mm});
            skLineSegment(sketch, "E289", {"start": v(-18.57, 6.4) * mm, "end": v(-21.18, 6.16) * mm});
            skLineSegment(sketch, "E290", {"start": v(-21.18, 6.16) * mm, "end": v(-23.5, 5.93) * mm});
            skLineSegment(sketch, "E291", {"start": v(-23.5, 5.93) * mm, "end": v(-24.27, 5.93) * mm});
            skLineSegment(sketch, "E292", {"start": v(-24.27, 5.93) * mm, "end": v(-25.56, 6.42) * mm});
            skLineSegment(sketch, "E293", {"start": v(-25.56, 6.42) * mm, "end": v(-27.18, 5.98) * mm});
            skLineSegment(sketch, "E294", {"start": v(-27.18, 5.98) * mm, "end": v(-28.95, 5.75) * mm});
            skLineSegment(sketch, "E295", {"start": v(-28.95, 5.75) * mm, "end": v(-30.94, 5.33) * mm});
            skLineSegment(sketch, "E296", {"start": v(-30.94, 5.33) * mm, "end": v(-31, 5.62) * mm});
            skLineSegment(sketch, "E297", {"start": v(-31, 5.62) * mm, "end": v(-31.6, 5.45) * mm});
            skLineSegment(sketch, "E298", {"start": v(-31.6, 5.45) * mm, "end": v(-31.63, 5) * mm});
            skSolve(sketch);
        }
        {
            var Q0;
            Q0 = qSketchRegion(id + "F10", true);
            extrude(context, id + "F11", {"entities" : qUnion([Q0]), "operationType" : NewBodyOperationType.REMOVE, "oppositeDirection" : true, "depth" : 2.54 * mm});
        }
    });
